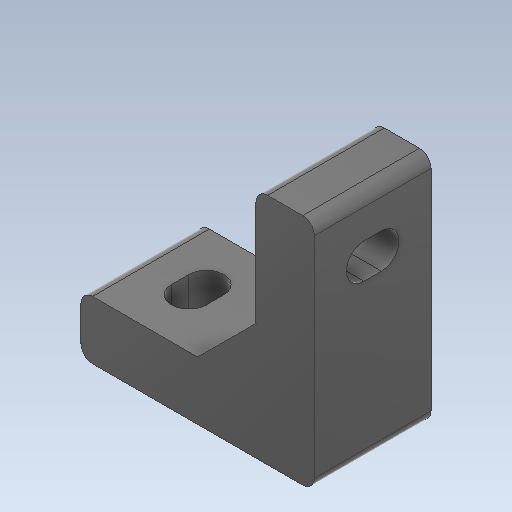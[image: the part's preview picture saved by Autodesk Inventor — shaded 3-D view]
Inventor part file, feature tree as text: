
AUTODESK INVENTOR PART (.ipt)
format: ipt  version: 2020 (Build 240168000, 168)  size: 180,224 bytes
history: native  units: mm
features: extrude x4, sketch x4, chamfer x1, fillet x1
ambient origin geometry x8: Origin, YZ Plane, XZ Plane, XY Plane, X Axis, Y Axis, Z Axis, Center Point
bodies: Solid1 (feature_tree)
feature tree (10):
  extrude  "Extrusion1"  Depth=40.0mm
  extrude  "Extrusion2"  Depth=40.0mm TaperAngle=0.0deg
  extrude  "Extrusion3"  Depth=3.0mm
  chamfer  "Chamfer1"  Distance=10.0mm
  fillet  "Fillet1"  [1 undecoded]
  extrude  "Extrusion4"  Depth=3.0mm
  sketch  "Sketch1"  dims[d0=10.0mm d1=40.0mm]
  sketch  "Sketch2"  dims[d2=40.0mm d3=40.0mm d4=0.0mm]
  sketch  "Sketch3"  dims[d5=6.0mm d6=3.0mm]
  sketch  "Sketch4"  dims[d7=10.0mm d8=10.0mm d9=0.0mm d10=0.0mm d11=3.0mm d12=6.0mm d13=10.0mm d14=10.0mm d15=0.0mm d16=0.0mm d17=10.0mm d18=2.0mm d19=45.0deg d20=2.0mm d21=20.0mm d22=0.0mm d23=0.0mm]
note: 1 required parameter value undecoded (feature->parameter linkage not recoverable at this tier; creation-order binding heuristic only, values carry confidence <= 0.55)
